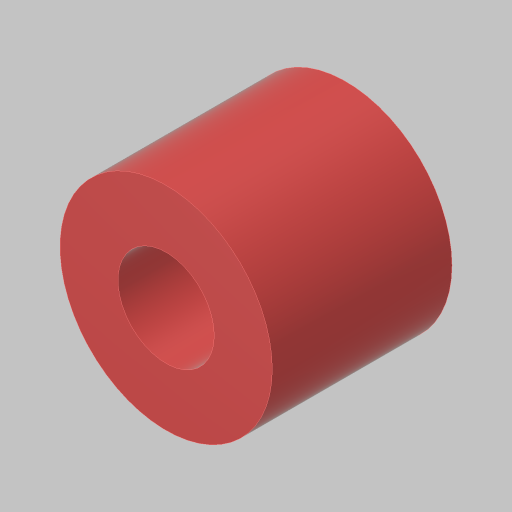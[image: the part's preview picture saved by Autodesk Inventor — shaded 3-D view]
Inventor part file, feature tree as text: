
AUTODESK INVENTOR PART (.ipt)
format: ipt  version: 2023.5 (Build 275446000, 446)  size: 111,616 bytes
history: native  units: in
note: dims shown in document units (in); Inventor stores cm internally (conversion verified against a paired STEP export)
features: extrude x1, sketch x1
ambient origin geometry x8: Origin, YZ Plane, XZ Plane, XY Plane, X Axis, Y Axis, Z Axis, Center Point
bodies: Solid1 (feature_tree)
feature tree (2):
  extrude  "Extrusion1"  Depth=0.7745in
  sketch  "Sketch1"  dims[d0=0.25in d1=0.415in d2=0.7745in d3=0.0in]
